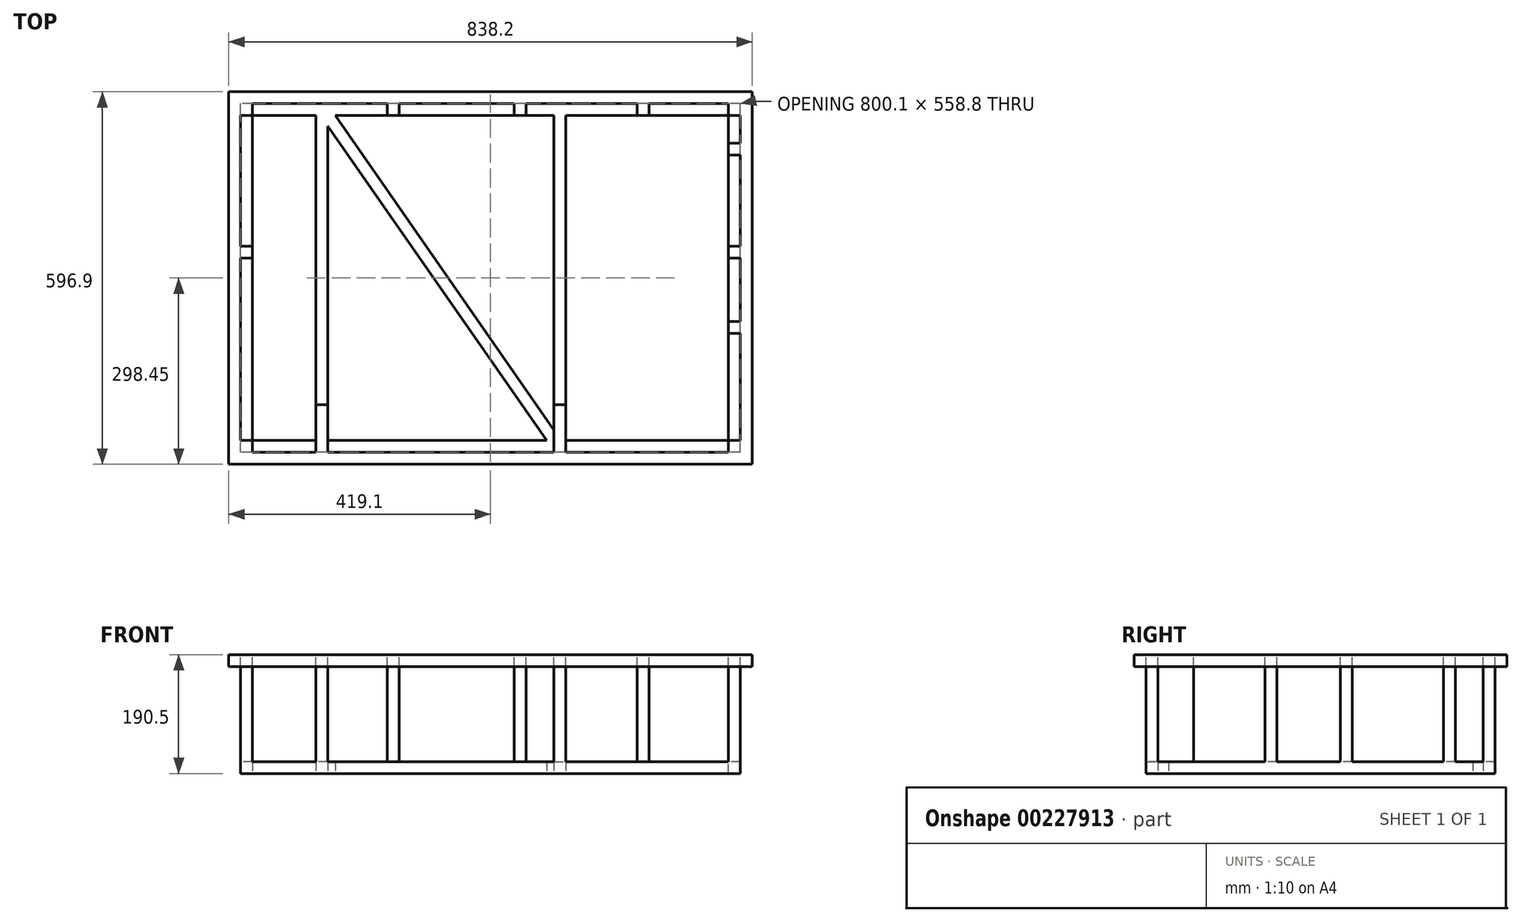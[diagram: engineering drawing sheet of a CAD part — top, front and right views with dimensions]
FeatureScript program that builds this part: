
annotation { "Feature Type Name" : "Feature", "Feature Type Description" : "" }
export const myFeature = defineFeature(function(context is Context, id is Id, definition is map)
    precondition{}
    {
        {
            var Q0;
            Q0=qCreatedBy(makeId("Top.planeOp"),FACE);
            var sketch = newSketch(context, id + "F0", { "sketchPlane" : qUnion([Q0])});
            skLineSegment(sketch, "E0.bottom", {"start": v(419.1, -298.45) * mm, "end": v(-419.1, -298.45) * mm});
            skLineSegment(sketch, "E0.top", {"start": v(419.1, 298.45) * mm, "end": v(-419.1, 298.45) * mm});
            skLineSegment(sketch, "E0.left", {"start": v(419.1, -298.45) * mm, "end": v(419.1, 298.45) * mm});
            skLineSegment(sketch, "E0.right", {"start": v(-419.1, -298.45) * mm, "end": v(-419.1, 298.45) * mm});
            skPoint(sketch, "E0.middle", {"position": v(0, 0) * mm});
            skSolve(sketch);
        }
        {
            var Q0;
            Q0=makeQuery(id+"F0.imprint","IMPRINT",FACE,{"disambiguationData":[TD([[makeQuery(id+"F0.imprint","IMPRINT",EDGE,{"derivedFrom":sQuery(id+"F0.wireOp",EDGE,"E0.bottom")}),-1.0]])]});
            extrude(context, id + "F1", {"entities" : qUnion([Q0]), "depth" : 19.05 * mm, "offsetDistance" : 25.4 * mm});
        }
        {
            var Q0;
            Q0=makeQuery(id+"F1.opExtrude","CAP_FACE",FACE,{"disambiguationData":[OSD([sQuery(id+"F0.wireOp",EDGE,"E0.bottom"),sQuery(id+"F0.wireOp",EDGE,"E0.top"),sQuery(id+"F0.wireOp",EDGE,"E0.left"),sQuery(id+"F0.wireOp",EDGE,"E0.right")])],"isStart":false});
            var sketch = newSketch(context, id + "F2", { "sketchPlane" : qUnion([Q0])});
            skLineSegment(sketch, "E1.0", {"start": v(400.05, -279.4) * mm, "end": v(-400.05, -279.4) * mm});
            skLineSegment(sketch, "E1.1", {"start": v(400.05, -279.4) * mm, "end": v(400.05, 279.4) * mm});
            skLineSegment(sketch, "E1.2", {"start": v(400.05, 279.4) * mm, "end": v(-400.05, 279.4) * mm});
            skLineSegment(sketch, "E1.3", {"start": v(-400.05, -279.4) * mm, "end": v(-400.05, 279.4) * mm});
            skSolve(sketch);
        }
        {
            var Q0;
            Q0=makeQuery(id+"F2.imprint","IMPRINT",FACE,{"disambiguationData":[TD([[makeQuery(id+"F2.imprint","IMPRINT",EDGE,{"derivedFrom":sQuery(id+"F2.wireOp",EDGE,"E1.0")}),-1.0]])]});
            extrude(context, id + "F3", {"entities" : qUnion([Q0]), "operationType" : NewBodyOperationType.REMOVE, "endBound" : BoundingType.THROUGH_ALL, "oppositeDirection" : true, "depth" : 25.4 * mm, "offsetDistance" : 25.4 * mm});
        }
        {
            var Q0;
            Q0=makeQuery(id+"F2.imprint","IMPRINT",FACE,{"disambiguationData":[TD([[makeQuery(id+"F2.imprint","IMPRINT",EDGE,{"derivedFrom":sQuery(id+"F2.wireOp",EDGE,"E1.0")}),-1.0]])]});
            var sketch = newSketch(context, id + "F4", { "sketchPlane" : qUnion([Q0])});
            skLineSegment(sketch, "E2.0", {"start": v(-381, -317.5) * mm, "end": v(-381, -260.35) * mm});
            skLineSegment(sketch, "E3.0", {"start": v(406.4, 260.35) * mm, "end": v(381, 260.35) * mm});
            skLineSegment(sketch, "E4.0", {"start": v(381, -317.5) * mm, "end": v(381, -260.35) * mm});
            skLineSegment(sketch, "E5.0", {"start": v(406.4, -260.35) * mm, "end": v(381, -260.35) * mm});
            skLineSegment(sketch, "E6.trimOffspring", {"start": v(-381, -260.35) * mm, "end": v(-406.4, -260.35) * mm});
            skLineSegment(sketch, "E7.trimOffspring", {"start": v(381, 260.35) * mm, "end": v(381, 317.5) * mm});
            skLineSegment(sketch, "E8.trimOffspring", {"start": v(-381, 260.35) * mm, "end": v(-406.4, 260.35) * mm});
            skLineSegment(sketch, "E9.trimOffspring", {"start": v(-381, 260.35) * mm, "end": v(-381, 317.5) * mm});
            skLineSegment(sketch, "E10.0", {"start": v(-177.8, -317.5) * mm, "end": v(-177.8, -298.45) * mm});
            skLineSegment(sketch, "E11.0", {"start": v(-158.75, -317.5) * mm, "end": v(-158.75, -298.45) * mm});
            skLineSegment(sketch, "E12", {"start": v(-177.8, -298.45) * mm, "end": v(-158.75, -298.45) * mm});
            skSolve(sketch);
        }
        {
            var Q0;
            {var subQ0=sQuery(id+"F4.wireOp",EDGE,"E8.trimOffspring");Q0=makeQuery(id+"F4.imprint","IMPRINT",FACE,{"disambiguationData":[TD([[makeQuery(id+"F4.imprint","IMPRINT",EDGE,{"derivedFrom":subQ0}),-1.0]])]});}
            var Q1;
            {var subQ0=sQuery(id+"F4.wireOp",EDGE,"E2.0");Q1=makeQuery(id+"F4.imprint","IMPRINT",FACE,{"disambiguationData":[TD([[makeQuery(id+"F4.imprint","IMPRINT",EDGE,{"derivedFrom":subQ0}),1.0]])]});}
            var Q2;
            {var subQ0=sQuery(id+"F4.wireOp",EDGE,"E3.0");Q2=makeQuery(id+"F4.imprint","IMPRINT",FACE,{"disambiguationData":[TD([[makeQuery(id+"F4.imprint","IMPRINT",EDGE,{"derivedFrom":subQ0}),-1.0]])]});}
            var Q3;
            {var subQ0=sQuery(id+"F4.wireOp",EDGE,"E4.0");Q3=makeQuery(id+"F4.imprint","IMPRINT",FACE,{"disambiguationData":[TD([[makeQuery(id+"F4.imprint","IMPRINT",EDGE,{"derivedFrom":subQ0}),-1.0]])]});}
            extrude(context, id + "F5", {"entities" : qUnion([Q0, Q1, Q2, Q3]), "operationType" : NewBodyOperationType.ADD, "oppositeDirection" : true, "depth" : 190.5 * mm, "offsetDistance" : 25.4 * mm});
        }
        {
            var Q0;
            Q0=makeQuery(id+"F2.imprint","IMPRINT",FACE,{"disambiguationData":[TD([[makeQuery(id+"F2.imprint","IMPRINT",EDGE,{"derivedFrom":sQuery(id+"F2.wireOp",EDGE,"E1.0")}),-1.0]])]});
            var sketch = newSketch(context, id + "F6", { "sketchPlane" : qUnion([Q0])});
            skLineSegment(sketch, "E13.left", {"start": v(-279.4, -203.2) * mm, "end": v(-279.4, -279.4) * mm});
            skLineSegment(sketch, "E13.right", {"start": v(-260.35, -203.2) * mm, "end": v(-260.35, -279.4) * mm});
            skLineSegment(sketch, "E14.0", {"start": v(-260.35, -203.2) * mm, "end": v(-279.4, -203.2) * mm});
            skLineSegment(sketch, "E15.0", {"start": v(406.4, -279.4) * mm, "end": v(-406.4, -279.4) * mm});
            skSolve(sketch);
        }
        {
            var Q0;
            Q0=makeQuery(id+"F6.imprint","IMPRINT",FACE,{"disambiguationData":[TD([[makeQuery(id+"F6.imprint","IMPRINT",EDGE,{"derivedFrom":sQuery(id+"F6.wireOp",EDGE,"E13.bottom")}),-1.0]])]});
            var Q1;
            {var subQ0=sQuery(id+"F6.wireOp",EDGE,"E13.left");Q1=makeQuery(id+"F6.imprint","IMPRINT",FACE,{"disambiguationData":[TD([[makeQuery(id+"F6.imprint","IMPRINT",EDGE,{"derivedFrom":subQ0}),1.0]])]});}
            extrude(context, id + "F7", {"entities" : qUnion([Q0, Q1]), "operationType" : NewBodyOperationType.ADD, "oppositeDirection" : true, "depth" : 190.5 * mm, "offsetDistance" : 25.4 * mm});
        }
        {
            var Q0;
            Q0=makeQuery(id+"F2.imprint","IMPRINT",FACE,{"disambiguationData":[TD([[makeQuery(id+"F2.imprint","IMPRINT",EDGE,{"derivedFrom":sQuery(id+"F2.wireOp",EDGE,"E1.0")}),1.0]])]});
            var sketch = newSketch(context, id + "F8", { "sketchPlane" : qUnion([Q0])});
            skLineSegment(sketch, "E16.0", {"start": v(-381, 31.75) * mm, "end": v(-381, 50.8) * mm});
            skLineSegment(sketch, "E17.0", {"start": v(406.4, 50.8) * mm, "end": v(381, 50.8) * mm});
            skLineSegment(sketch, "E18.0", {"start": v(381, 31.75) * mm, "end": v(381, 50.8) * mm});
            skLineSegment(sketch, "E19.0", {"start": v(19.05, -317.5) * mm, "end": v(19.05, 286.13) * mm});
            skLineSegment(sketch, "E20.0", {"start": v(406.4, 260.35) * mm, "end": v(381, 260.35) * mm});
            skLineSegment(sketch, "E21.0", {"start": v(406.4, 31.75) * mm, "end": v(381, 31.75) * mm});
            skLineSegment(sketch, "E22.0", {"start": v(0, -317.5) * mm, "end": v(0, 289.85) * mm});
            skLineSegment(sketch, "E23.trimOffspring", {"start": v(-381, 50.8) * mm, "end": v(-406.4, 50.8) * mm});
            skLineSegment(sketch, "E24.trimOffspring", {"start": v(-381, 260.35) * mm, "end": v(-381, 317.5) * mm});
            skLineSegment(sketch, "E25.trimOffspring", {"start": v(-381, 31.75) * mm, "end": v(-406.4, 31.75) * mm});
            skLineSegment(sketch, "E26.trimOffspring", {"start": v(-381, 260.35) * mm, "end": v(-406.4, 260.35) * mm});
            skLineSegment(sketch, "E27.trimOffspring", {"start": v(19.05, 260.35) * mm, "end": v(0, 260.35) * mm});
            skLineSegment(sketch, "E28.trimOffspring", {"start": v(19.05, 50.8) * mm, "end": v(0, 50.8) * mm});
            skLineSegment(sketch, "E29.trimOffspring", {"start": v(19.05, 31.75) * mm, "end": v(0, 31.75) * mm});
            skLineSegment(sketch, "E30.trimOffspring", {"start": v(381, 260.35) * mm, "end": v(381, 317.5) * mm});
            skSolve(sketch);
        }
        {
            var Q0;
            Q0=makeQuery(id+"F8.imprint","IMPRINT",FACE,{"disambiguationData":[TD([[makeQuery(id+"F8.imprint","IMPRINT",EDGE,{"derivedFrom":sQuery(id+"F8.wireOp",EDGE,"E16.0")}),1.0]])]});
            var Q1;
            {var subQ0=sQuery(id+"F8.wireOp",EDGE,"92bb0c61-4761-4d68-9f9f-d430d65edb0f.trimOffspring");Q1=makeQuery(id+"F8.imprint","IMPRINT",FACE,{"disambiguationData":[TD([[makeQuery(id+"F8.imprint","IMPRINT",EDGE,{"derivedFrom":subQ0}),-1.0]])]});}
            var Q2;
            {var subQ0=sQuery(id+"F8.wireOp",EDGE,"E17.0");Q2=makeQuery(id+"F8.imprint","IMPRINT",FACE,{"disambiguationData":[TD([[makeQuery(id+"F8.imprint","IMPRINT",EDGE,{"derivedFrom":subQ0}),1.0]])]});}
            extrude(context, id + "F9", {"entities" : qUnion([Q0, Q1, Q2]), "operationType" : NewBodyOperationType.ADD, "oppositeDirection" : true, "depth" : 190.5 * mm, "offsetDistance" : 25.4 * mm});
        }
        {
            var Q0;
            Q0=makeQuery(id+"F5.opExtrude","SWEPT_FACE",FACE,{"disambiguationData":[OSD([sQuery(id+"F4.wireOp",EDGE,"E8.trimOffspring")])]});
            var sketch = newSketch(context, id + "F10", { "sketchPlane" : qUnion([Q0])});
            skLineSegment(sketch, "E31.top", {"start": v(-381, -152.4) * mm, "end": v(-400.05, -152.4) * mm});
            skSolve(sketch);
        }
        {
            var Q0;
            Q0=makeQuery(id+"F5.opExtrude","SWEPT_FACE",FACE,{"disambiguationData":[OSD([sQuery(id+"F4.wireOp",EDGE,"E3.0")])]});
            var sketch = newSketch(context, id + "F11", { "sketchPlane" : qUnion([Q0])});
            skSolve(sketch);
        }
        {
            var Q0;
            {var subQ0=sQuery(id+"F10.wireOp",EDGE,"E31.top");Q0=makeQuery(id+"F10.imprint","IMPRINT",FACE,{"disambiguationData":[TD([[makeQuery(id+"F10.imprint","IMPRINT",EDGE,{"derivedFrom":subQ0}),1.0]])]});}
            var Q1;
            Q1=makeQuery(id+"FXD4YSxns08IY23_10.boolean.opBoolean","MERGE",FACE,{"derivedFrom":[makeQuery(id+"F5.opExtrude","SWEPT_FACE",FACE,{"disambiguationData":[OSD([sQuery(id+"F4.wireOp",EDGE,"E6.trimOffspring")])]}),makeQuery(id+"FXD4YSxns08IY23_10.opExtrude","SWEPT_FACE",FACE,{"disambiguationData":[OSD([sQuery(id+"F4.wireOp",EDGE,"E4.0"),sQuery(id+"F4.wireOp",EDGE,"E5.0")])]})]});
            extrude(context, id + "F12", {"entities" : qUnion([Q0]), "operationType" : NewBodyOperationType.ADD, "endBound" : BoundingType.UP_TO_SURFACE, "depth" : 25.4 * mm, "endBoundEntityFace" : qUnion([Q1]), "offsetDistance" : 25.4 * mm});
        }
        {
            var Q0;
            Q0=makeQuery(id+"F2.imprint","IMPRINT",FACE,{"disambiguationData":[TD([[makeQuery(id+"F2.imprint","IMPRINT",EDGE,{"derivedFrom":sQuery(id+"F2.wireOp",EDGE,"E1.0")}),-1.0]])]});
            var sketch = newSketch(context, id + "F13", { "sketchPlane" : qUnion([Q0])});
            skLineSegment(sketch, "E32.0", {"start": v(120.65, -317.5) * mm, "end": v(120.65, -203.2) * mm});
            skLineSegment(sketch, "E33.0", {"start": v(101.6, -317.5) * mm, "end": v(101.6, -203.2) * mm});
            skLineSegment(sketch, "E34.0", {"start": v(120.65, -203.2) * mm, "end": v(101.6, -203.2) * mm});
            skSolve(sketch);
        }
        {
            var Q0;
            {var subQ0=sQuery(id+"F13.wireOp",EDGE,"E32.0");Q0=makeQuery(id+"F13.imprint","IMPRINT",FACE,{"disambiguationData":[TD([[makeQuery(id+"F13.imprint","IMPRINT",EDGE,{"derivedFrom":subQ0}),1.0]])]});}
            var Q1;
            {var subQ0=sQuery(id+"F6.wireOp",EDGE,"E14.0");var subQ1=sQuery(id+"F4.wireOp",EDGE,"E8.trimOffspring");var subQ2=sQuery(id+"F4.wireOp",EDGE,"E4.0");var subQ3=sQuery(id+"F4.wireOp",EDGE,"E5.0");var subQ4=sQuery(id+"F8.wireOp",EDGE,"3b298be8-fb02-4c87-a49b-3ff32759ba27.trimOffspring");var subQ5=sQuery(id+"F4.wireOp",EDGE,"E9.trimOffspring");var subQ6=sQuery(id+"F2.wireOp",EDGE,"E1.2");var subQ7=sQuery(id+"F2.wireOp",EDGE,"E1.3");var subQ8=sQuery(id+"F2.wireOp",EDGE,"E1.1");var subQ9=sQuery(id+"F2.wireOp",EDGE,"E1.0");Q1=makeQuery(id+"FpkB6zeeMxbo54k_1.boolean.opBoolean","MERGE",FACE,{"derivedFrom":[makeQuery(id+"F12.boolean.opBoolean","MERGE",FACE,{"derivedFrom":[makeQuery(id+"F9.opExtrude","CAP_FACE",FACE,{"disambiguationData":[OSD([subQ7,sQuery(id+"F8.wireOp",EDGE,"E16.0"),sQuery(id+"F8.wireOp",EDGE,"E23.trimOffspring"),sQuery(id+"F8.wireOp",EDGE,"E25.trimOffspring")])],"isStart":false}),makeQuery(id+"FXD4YSxns08IY23_10.boolean.opBoolean","MERGE",FACE,{"derivedFrom":[makeQuery(id+"F5.opExtrude","CAP_FACE",FACE,{"disambiguationData":[OSD([subQ9,subQ7,sQuery(id+"F4.wireOp",EDGE,"E2.0"),sQuery(id+"F4.wireOp",EDGE,"E6.trimOffspring")])],"isStart":false}),makeQuery(id+"F7.opExtrude","CAP_FACE",FACE,{"disambiguationData":[OSD([sQuery(id+"F6.wireOp",EDGE,"E13.left"),sQuery(id+"F6.wireOp",EDGE,"E13.right"),subQ0,sQuery(id+"F6.wireOp",EDGE,"E15.0")])],"isStart":false}),makeQuery(id+"FrElrkVLBZXkbWn_13.boolean.opBoolean","MERGE",FACE,{"derivedFrom":[makeQuery(id+"F5.opExtrude","CAP_FACE",FACE,{"disambiguationData":[OSD([subQ9,subQ8,subQ2,subQ3])],"isStart":false}),makeQuery(id+"F9.opExtrude","CAP_FACE",FACE,{"disambiguationData":[OSD([subQ8,sQuery(id+"F8.wireOp",EDGE,"E17.0"),sQuery(id+"F8.wireOp",EDGE,"E18.0"),sQuery(id+"F8.wireOp",EDGE,"E21.0")])],"isStart":false}),makeQuery(id+"Fi0JkrTjfxZnNrc_13.boolean.opBoolean","MERGE",FACE,{"derivedFrom":[makeQuery(id+"F5.opExtrude","CAP_FACE",FACE,{"disambiguationData":[OSD([subQ8,subQ6,sQuery(id+"F4.wireOp",EDGE,"E3.0"),sQuery(id+"F4.wireOp",EDGE,"E7.trimOffspring")])],"isStart":false}),makeQuery(id+"FCnJRw7mSyagZAr_13.boolean.opBoolean","MERGE",FACE,{"derivedFrom":[makeQuery(id+"F5.opExtrude","CAP_FACE",FACE,{"disambiguationData":[OSD([subQ6,subQ7,subQ1,subQ5])],"isStart":false}),makeQuery(id+"F9.opExtrude","CAP_FACE",FACE,{"disambiguationData":[OSD([subQ6,sQuery(id+"F8.wireOp",EDGE,"92bb0c61-4761-4d68-9f9f-d430d65edb0f.trimOffspring"),subQ4,sQuery(id+"F8.wireOp",EDGE,"E27.trimOffspring")])],"isStart":false}),makeQuery(id+"FCnJRw7mSyagZAr_13.opExtrude","SWEPT_FACE",FACE,{"disambiguationData":[OSD([subQ5])]})]}),makeQuery(id+"Fi0JkrTjfxZnNrc_13.opExtrude","SWEPT_FACE",FACE,{"disambiguationData":[OSD([subQ4])]})]}),makeQuery(id+"FrElrkVLBZXkbWn_13.opExtrude","SWEPT_FACE",FACE,{"disambiguationData":[OSD([subQ3])]})]}),makeQuery(id+"FXD4YSxns08IY23_10.opExtrude","SWEPT_FACE",FACE,{"disambiguationData":[OSD([subQ2])]})]}),makeQuery(id+"F12.opExtrude","SWEPT_FACE",FACE,{"disambiguationData":[OSD([subQ1])]})]}),makeQuery(id+"FpkB6zeeMxbo54k_1.opExtrude","SWEPT_FACE",FACE,{"disambiguationData":[OSD([subQ0])]})]});}
            extrude(context, id + "F14", {"entities" : qUnion([Q0]), "operationType" : NewBodyOperationType.ADD, "endBound" : BoundingType.UP_TO_SURFACE, "oppositeDirection" : true, "depth" : 25.4 * mm, "endBoundEntityFace" : qUnion([Q1]), "offsetDistance" : 25.4 * mm});
        }
        {
            var Q0;
            Q0=makeQuery(id+"F2.imprint","IMPRINT",FACE,{"disambiguationData":[TD([[makeQuery(id+"F2.imprint","IMPRINT",EDGE,{"derivedFrom":sQuery(id+"F2.wireOp",EDGE,"E1.0")}),-1.0]])]});
            var sketch = newSketch(context, id + "F15", { "sketchPlane" : qUnion([Q0])});
            skLineSegment(sketch, "E35.0", {"start": v(381, -88.9) * mm, "end": v(381, -69.85) * mm});
            skLineSegment(sketch, "E36.0", {"start": v(400.05, -88.9) * mm, "end": v(381, -88.9) * mm});
            skLineSegment(sketch, "E37.0", {"start": v(400.05, -69.85) * mm, "end": v(381, -69.85) * mm});
            skLineSegment(sketch, "E38.0", {"start": v(400.05, 196.85) * mm, "end": v(381, 196.85) * mm});
            skLineSegment(sketch, "E39.0", {"start": v(400.05, 215.9) * mm, "end": v(381, 215.9) * mm});
            skLineSegment(sketch, "E40.trimOffspring", {"start": v(381, 196.85) * mm, "end": v(381, 215.9) * mm});
            skLineSegment(sketch, "E41.0", {"start": v(400.05, 196.85) * mm, "end": v(400.05, 215.9) * mm});
            skLineSegment(sketch, "E42.0", {"start": v(400.05, -88.9) * mm, "end": v(400.05, -69.85) * mm});
            skSolve(sketch);
        }
        {
            var Q0;
            {var subQ0=sQuery(id+"F4.wireOp",EDGE,"E3.0");Q0=makeQuery(id+"F11.imprint","IMPRINT",FACE,{"disambiguationData":[TD([[makeQuery(id+"F11.imprint","IMPRINT",EDGE,{"derivedFrom":makeQuery(id+"F5.opExtrude","CAP_EDGE",EDGE,{"disambiguationData":[OSD([subQ0])],"isStart":true})}),1.0]])]});}
            var sketch = newSketch(context, id + "F16", { "sketchPlane" : qUnion([Q0])});
            skLineSegment(sketch, "E43.0", {"start": v(400.05, -152.4) * mm, "end": v(381, -152.4) * mm});
            skSolve(sketch);
        }
        {
            var Q0;
            {var subQ0=sQuery(id+"F16.wireOp",EDGE,"E43.0");Q0=makeQuery(id+"F16.imprint","IMPRINT",FACE,{"disambiguationData":[TD([[makeQuery(id+"F16.imprint","IMPRINT",EDGE,{"derivedFrom":subQ0}),1.0]])]});}
            var Q1;
            Q1=makeQuery(id+"F5.opExtrude","SWEPT_FACE",FACE,{"disambiguationData":[OSD([sQuery(id+"F4.wireOp",EDGE,"E5.0")])]});
            extrude(context, id + "F17", {"entities" : qUnion([Q0]), "operationType" : NewBodyOperationType.ADD, "endBound" : BoundingType.UP_TO_SURFACE, "depth" : 25.4 * mm, "endBoundEntityFace" : qUnion([Q1]), "offsetDistance" : 25.4 * mm});
        }
        {
            var Q0;
            {var subQ0=sQuery(id+"F4.wireOp",EDGE,"E9.trimOffspring");Q0=makeQuery(id+"F12.boolean.opBoolean","MERGE",FACE,{"derivedFrom":[makeQuery(id+"F5.opExtrude","SWEPT_FACE",FACE,{"disambiguationData":[OSD([sQuery(id+"F4.wireOp",EDGE,"E2.0")])]}),makeQuery(id+"F5.opExtrude","SWEPT_FACE",FACE,{"disambiguationData":[OSD([subQ0])]}),makeQuery(id+"F9.opExtrude","SWEPT_FACE",FACE,{"disambiguationData":[OSD([sQuery(id+"F8.wireOp",EDGE,"E16.0")])]}),makeQuery(id+"F12.opExtrude","SWEPT_FACE",FACE,{"disambiguationData":[OSD([sQuery(id+"F4.wireOp",EDGE,"E8.trimOffspring"),subQ0])]})]});}
            var sketch = newSketch(context, id + "F18", { "sketchPlane" : qUnion([Q0])});
            skLineSegment(sketch, "E44.0", {"start": v(260.35, -152.4) * mm, "end": v(279.4, -152.4) * mm});
            skLineSegment(sketch, "E45.0", {"start": v(260.35, -171.45) * mm, "end": v(260.35, -152.4) * mm});
            skSolve(sketch);
        }
        {
            var Q0;
            {var subQ0=sQuery(id+"F18.wireOp",EDGE,"E44.0");Q0=makeQuery(id+"F18.imprint","IMPRINT",FACE,{"disambiguationData":[TD([[makeQuery(id+"F18.imprint","IMPRINT",EDGE,{"derivedFrom":subQ0}),-1.0]])]});}
            var Q1;
            {var subQ0=sQuery(id+"F4.wireOp",EDGE,"E7.trimOffspring");Q1=makeQuery(id+"F17.boolean.opBoolean","MERGE",FACE,{"derivedFrom":[makeQuery(id+"F5.opExtrude","SWEPT_FACE",FACE,{"disambiguationData":[OSD([sQuery(id+"F4.wireOp",EDGE,"E4.0")])]}),makeQuery(id+"F5.opExtrude","SWEPT_FACE",FACE,{"disambiguationData":[OSD([subQ0])]}),makeQuery(id+"F9.opExtrude","SWEPT_FACE",FACE,{"disambiguationData":[OSD([sQuery(id+"F8.wireOp",EDGE,"E18.0")])]}),makeQuery(id+"F17.opExtrude","SWEPT_FACE",FACE,{"disambiguationData":[OSD([sQuery(id+"F4.wireOp",EDGE,"E3.0"),subQ0])]})]});}
            extrude(context, id + "F19", {"entities" : qUnion([Q0]), "operationType" : NewBodyOperationType.ADD, "endBound" : BoundingType.UP_TO_SURFACE, "depth" : 25.4 * mm, "endBoundEntityFace" : qUnion([Q1]), "offsetDistance" : 25.4 * mm});
        }
        {
            var Q0;
            {var subQ1=sQuery(id+"F2.wireOp",EDGE,"E1.0");var subQ3=sQuery(id+"F4.wireOp",EDGE,"E4.0");var subQ5=sQuery(id+"F8.wireOp",EDGE,"E18.0");var subQ19=sQuery(id+"F4.wireOp",EDGE,"E7.trimOffspring");var subQ20=makeQuery(id+"F5.opExtrude","SWEPT_FACE",FACE,{"disambiguationData":[OSD([subQ19])]});var subQ23=makeQuery(id+"F5.opExtrude","SWEPT_FACE",FACE,{"disambiguationData":[OSD([subQ3])]});var subQ24=sQuery(id+"F4.wireOp",EDGE,"E3.0");var subQ25=makeQuery(id+"F9.opExtrude","SWEPT_FACE",FACE,{"disambiguationData":[OSD([subQ5])]});var subQ26=makeQuery(id+"F17.opExtrude","SWEPT_FACE",FACE,{"disambiguationData":[OSD([subQ24,subQ19])]});Q0=makeQuery(id+"F19.boolean.opBoolean","SPLIT",FACE,{"disambiguationData":[TD([makeQuery(id+"F3.boolean.opBoolean","COPY",FACE,{"derivedFrom":makeQuery(id+"F3.opExtrude","SWEPT_FACE",FACE,{"disambiguationData":[OSD([subQ1])]})})])],"derivedFrom":makeQuery(id+"F17.boolean.opBoolean","MERGE",FACE,{"derivedFrom":[subQ23,subQ20,subQ25,subQ26]})});}
            var sketch = newSketch(context, id + "F20", { "sketchPlane" : qUnion([Q0])});
            skLineSegment(sketch, "E46.0", {"start": v(279.4, -152.4) * mm, "end": v(260.35, -152.4) * mm});
            skLineSegment(sketch, "E47.0", {"start": v(260.35, -171.45) * mm, "end": v(260.35, -152.4) * mm});
            skSolve(sketch);
        }
        {
            var Q0;
            {var subQ0=sQuery(id+"F20.wireOp",EDGE,"E46.0");Q0=makeQuery(id+"F20.imprint","IMPRINT",FACE,{"disambiguationData":[TD([[makeQuery(id+"F20.imprint","IMPRINT",EDGE,{"derivedFrom":subQ0}),1.0]])]});}
            var Q1;
            {var subQ0=sQuery(id+"F8.wireOp",EDGE,"E16.0");var subQ1=makeQuery(id+"F9.opExtrude","SWEPT_FACE",FACE,{"disambiguationData":[OSD([subQ0])]});var subQ2=sQuery(id+"F4.wireOp",EDGE,"E8.trimOffspring");var subQ4=sQuery(id+"F2.wireOp",EDGE,"E1.0");var subQ6=sQuery(id+"F4.wireOp",EDGE,"E2.0");var subQ11=sQuery(id+"F4.wireOp",EDGE,"E9.trimOffspring");var subQ12=makeQuery(id+"F5.opExtrude","SWEPT_FACE",FACE,{"disambiguationData":[OSD([subQ11])]});var subQ23=makeQuery(id+"F5.opExtrude","SWEPT_FACE",FACE,{"disambiguationData":[OSD([subQ6])]});var subQ26=makeQuery(id+"F12.opExtrude","SWEPT_FACE",FACE,{"disambiguationData":[OSD([subQ2,subQ11])]});Q1=makeQuery(id+"F19.boolean.opBoolean","SPLIT",FACE,{"disambiguationData":[TD([makeQuery(id+"F3.boolean.opBoolean","COPY",FACE,{"derivedFrom":makeQuery(id+"F3.opExtrude","SWEPT_FACE",FACE,{"disambiguationData":[OSD([subQ4])]})})])],"derivedFrom":makeQuery(id+"F12.boolean.opBoolean","MERGE",FACE,{"derivedFrom":[subQ23,subQ12,subQ1,subQ26]})});}
            extrude(context, id + "F21", {"entities" : qUnion([Q0]), "operationType" : NewBodyOperationType.ADD, "endBound" : BoundingType.UP_TO_SURFACE, "depth" : 25.4 * mm, "endBoundEntityFace" : qUnion([Q1]), "offsetDistance" : 25.4 * mm});
        }
        {
            var Q0;
            Q0=makeQuery(id+"F15.imprint","IMPRINT",FACE,{"disambiguationData":[TD([[makeQuery(id+"F15.imprint","IMPRINT",EDGE,{"derivedFrom":sQuery(id+"F15.wireOp",EDGE,"E35.0")}),-1.0]])]});
            var Q1;
            {var subQ2=sQuery(id+"F4.wireOp",EDGE,"E5.0");Q1=makeQuery(id+"F17.boolean.opBoolean","SPLIT",FACE,{"disambiguationData":[TD([makeQuery(id+"F5.opExtrude","SWEPT_FACE",FACE,{"disambiguationData":[OSD([subQ2])]})])],"derivedFrom":makeQuery(id+"F17.opExtrude","SWEPT_FACE",FACE,{"disambiguationData":[OSD([sQuery(id+"F16.wireOp",EDGE,"E43.0")])]})});}
            extrude(context, id + "F22", {"entities" : qUnion([Q0, Q1]), "operationType" : NewBodyOperationType.ADD, "endBound" : BoundingType.UP_TO_NEXT, "oppositeDirection" : true, "depth" : 25.4 * mm, "offsetDistance" : 25.4 * mm});
        }
        {
            var Q0;
            Q0 = qSketchRegion(id + "F15", true);
            extrude(context, id + "F23", {"entities" : qUnion([Q0]), "operationType" : NewBodyOperationType.ADD, "endBound" : BoundingType.UP_TO_NEXT, "oppositeDirection" : true, "depth" : 25.4 * mm, "offsetDistance" : 25.4 * mm});
        }
        {
            var Q0;
            Q0=makeQuery(id+"F14.opExtrude","SWEPT_FACE",FACE,{"disambiguationData":[OSD([sQuery(id+"F13.wireOp",EDGE,"E34.0")])]});
            var sketch = newSketch(context, id + "F24", { "sketchPlane" : qUnion([Q0])});
            skLineSegment(sketch, "E48.0", {"start": v(-101.6, -152.4) * mm, "end": v(-120.65, -152.4) * mm});
            skSolve(sketch);
        }
        {
            var Q0;
            {var subQ0=sQuery(id+"F24.wireOp",EDGE,"E48.0");Q0=makeQuery(id+"F24.imprint","IMPRINT",FACE,{"disambiguationData":[TD([[makeQuery(id+"F24.imprint","IMPRINT",EDGE,{"derivedFrom":subQ0}),1.0]])]});}
            extrude(context, id + "F25", {"entities" : qUnion([Q0]), "operationType" : NewBodyOperationType.ADD, "endBound" : BoundingType.UP_TO_NEXT, "depth" : 25.4 * mm, "offsetDistance" : 25.4 * mm});
        }
        {
            var Q0;
            Q0=makeQuery(id+"F7.opExtrude","SWEPT_FACE",FACE,{"disambiguationData":[OSD([sQuery(id+"F6.wireOp",EDGE,"E14.0")])]});
            var sketch = newSketch(context, id + "F26", { "sketchPlane" : qUnion([Q0])});
            skLineSegment(sketch, "E49.0", {"start": v(260.35, -152.4) * mm, "end": v(279.4, -152.4) * mm});
            skSolve(sketch);
        }
        {
            var Q0;
            {var subQ0=sQuery(id+"F26.wireOp",EDGE,"E49.0");Q0=makeQuery(id+"F26.imprint","IMPRINT",FACE,{"disambiguationData":[TD([[makeQuery(id+"F26.imprint","IMPRINT",EDGE,{"derivedFrom":subQ0}),-1.0]])]});}
            extrude(context, id + "F27", {"entities" : qUnion([Q0]), "operationType" : NewBodyOperationType.ADD, "endBound" : BoundingType.UP_TO_NEXT, "depth" : 25.4 * mm, "offsetDistance" : 25.4 * mm});
        }
        {
            var Q0;
            Q0=makeQuery(id+"F2.imprint","IMPRINT",FACE,{"disambiguationData":[TD([[makeQuery(id+"F2.imprint","IMPRINT",EDGE,{"derivedFrom":sQuery(id+"F2.wireOp",EDGE,"E1.0")}),-1.0]])]});
            var sketch = newSketch(context, id + "F28", { "sketchPlane" : qUnion([Q0])});
            skLineSegment(sketch, "E50.0", {"start": v(254, 260.35) * mm, "end": v(234.95, 260.35) * mm});
            skLineSegment(sketch, "E51.0", {"start": v(-165.1, 260.35) * mm, "end": v(-165.1, 279.4) * mm});
            skLineSegment(sketch, "E52.0", {"start": v(-146.05, 260.35) * mm, "end": v(-146.05, 279.4) * mm});
            skLineSegment(sketch, "E53.0", {"start": v(254, 260.35) * mm, "end": v(254, 279.4) * mm});
            skLineSegment(sketch, "E54.0", {"start": v(234.95, 260.35) * mm, "end": v(234.95, 279.4) * mm});
            skLineSegment(sketch, "E55.0", {"start": v(57.15, 260.35) * mm, "end": v(57.15, 279.4) * mm});
            skLineSegment(sketch, "E56.0", {"start": v(38.1, 260.35) * mm, "end": v(38.1, 279.4) * mm});
            skLineSegment(sketch, "E57.trimOffspring", {"start": v(-146.05, 260.35) * mm, "end": v(-165.1, 260.35) * mm});
            skLineSegment(sketch, "E58.trimOffspring", {"start": v(57.15, 260.35) * mm, "end": v(38.1, 260.35) * mm});
            skSolve(sketch);
        }
        {
            var Q0;
            {var subQ0=sQuery(id+"F28.wireOp",EDGE,"E51.0");Q0=makeQuery(id+"F28.imprint","IMPRINT",FACE,{"disambiguationData":[TD([[makeQuery(id+"F28.imprint","IMPRINT",EDGE,{"derivedFrom":subQ0}),-1.0]])]});}
            var Q1;
            {var subQ0=sQuery(id+"F28.wireOp",EDGE,"E55.0");Q1=makeQuery(id+"F28.imprint","IMPRINT",FACE,{"disambiguationData":[TD([[makeQuery(id+"F28.imprint","IMPRINT",EDGE,{"derivedFrom":subQ0}),1.0]])]});}
            var Q2;
            Q2=makeQuery(id+"F28.imprint","IMPRINT",FACE,{"disambiguationData":[TD([[makeQuery(id+"F28.imprint","IMPRINT",EDGE,{"derivedFrom":sQuery(id+"F28.wireOp",EDGE,"E50.0")}),-1.0]])]});
            extrude(context, id + "F29", {"entities" : qUnion([Q0, Q1, Q2]), "operationType" : NewBodyOperationType.ADD, "endBound" : BoundingType.UP_TO_NEXT, "oppositeDirection" : true, "depth" : 25.4 * mm, "offsetDistance" : 25.4 * mm});
        }
        {
            var Q0;
            {var subQ0=sQuery(id+"F6.wireOp",EDGE,"E14.0");var subQ1=sQuery(id+"F8.wireOp",EDGE,"E25.trimOffspring");var subQ2=sQuery(id+"F8.wireOp",EDGE,"E23.trimOffspring");var subQ3=sQuery(id+"F8.wireOp",EDGE,"E16.0");var subQ4=sQuery(id+"F4.wireOp",EDGE,"E9.trimOffspring");var subQ5=sQuery(id+"F4.wireOp",EDGE,"E8.trimOffspring");var subQ6=sQuery(id+"F4.wireOp",EDGE,"E6.trimOffspring");var subQ7=sQuery(id+"F4.wireOp",EDGE,"E2.0");var subQ8=sQuery(id+"F2.wireOp",EDGE,"E1.3");var subQ9=sQuery(id+"F2.wireOp",EDGE,"E1.2");var subQ10=sQuery(id+"F2.wireOp",EDGE,"E1.0");var subQ11=sQuery(id+"F8.wireOp",EDGE,"E18.0");var subQ12=sQuery(id+"F4.wireOp",EDGE,"E7.trimOffspring");var subQ13=sQuery(id+"F4.wireOp",EDGE,"E4.0");var subQ14=sQuery(id+"F4.wireOp",EDGE,"E3.0");var subQ15=sQuery(id+"F2.wireOp",EDGE,"E1.1");Q0=makeQuery(id+"F27.boolean.opBoolean","MERGE",FACE,{"derivedFrom":[makeQuery(id+"F25.boolean.opBoolean","MERGE",FACE,{"derivedFrom":[makeQuery(id+"F21.boolean.opBoolean","MERGE",FACE,{"derivedFrom":[makeQuery(id+"F7.opExtrude","CAP_FACE",FACE,{"disambiguationData":[OSD([sQuery(id+"F6.wireOp",EDGE,"E13.left"),sQuery(id+"F6.wireOp",EDGE,"E13.right"),subQ0,sQuery(id+"F6.wireOp",EDGE,"E15.0")])],"isStart":false}),makeQuery(id+"F14.opExtrude","CAP_FACE",FACE,{"disambiguationData":[OSD([subQ10,subQ9,subQ8,subQ7,subQ6,subQ5,subQ4,subQ3,subQ2,subQ1])],"isStart":false}),makeQuery(id+"F19.boolean.opBoolean","MERGE",FACE,{"derivedFrom":[makeQuery(id+"F12.boolean.opBoolean","MERGE",FACE,{"derivedFrom":[makeQuery(id+"F5.opExtrude","CAP_FACE",FACE,{"disambiguationData":[OSD([subQ10,subQ8,subQ7,subQ6])],"isStart":false}),makeQuery(id+"F5.opExtrude","CAP_FACE",FACE,{"disambiguationData":[OSD([subQ9,subQ8,subQ5,subQ4])],"isStart":false}),makeQuery(id+"F9.opExtrude","CAP_FACE",FACE,{"disambiguationData":[OSD([subQ8,subQ3,subQ2,subQ1])],"isStart":false}),makeQuery(id+"F12.opExtrude","SWEPT_FACE",FACE,{"disambiguationData":[OSD([subQ5])]})]}),makeQuery(id+"F17.boolean.opBoolean","MERGE",FACE,{"derivedFrom":[makeQuery(id+"F5.opExtrude","CAP_FACE",FACE,{"disambiguationData":[OSD([subQ15,subQ9,subQ14,subQ12])],"isStart":false}),makeQuery(id+"F5.opExtrude","CAP_FACE",FACE,{"disambiguationData":[OSD([subQ10,subQ15,subQ13,sQuery(id+"F4.wireOp",EDGE,"E5.0")])],"isStart":false}),makeQuery(id+"F9.opExtrude","CAP_FACE",FACE,{"disambiguationData":[OSD([subQ15,sQuery(id+"F8.wireOp",EDGE,"E17.0"),subQ11,sQuery(id+"F8.wireOp",EDGE,"E21.0")])],"isStart":false}),makeQuery(id+"F17.opExtrude","SWEPT_FACE",FACE,{"disambiguationData":[OSD([subQ14])]})]}),makeQuery(id+"F19.opExtrude","SWEPT_FACE",FACE,{"disambiguationData":[OSD([subQ7,subQ5,subQ4,subQ3])]})]}),makeQuery(id+"F21.opExtrude","SWEPT_FACE",FACE,{"disambiguationData":[OSD([subQ14,subQ13,subQ12,subQ11])]})]}),makeQuery(id+"F25.opExtrude","SWEPT_FACE",FACE,{"disambiguationData":[OSD([subQ10,subQ9,subQ8,subQ7,subQ6,subQ5,subQ4,subQ3,subQ2,subQ1,sQuery(id+"F13.wireOp",EDGE,"E34.0")])]})]}),makeQuery(id+"F27.opExtrude","SWEPT_FACE",FACE,{"disambiguationData":[OSD([subQ0])]})]});}
            var sketch = newSketch(context, id + "F30", { "sketchPlane" : qUnion([Q0])});
            skLineSegment(sketch, "E59.0", {"start": v(-268.17, -254.91) * mm, "end": v(93.78, 265.79) * mm});
            skLineSegment(sketch, "E60.0", {"start": v(-252.53, -265.79) * mm, "end": v(109.42, 254.91) * mm});
            skSolve(sketch);
        }
        {
            var Q0;
            {var subQ26=sQuery(id+"F6.wireOp",EDGE,"E14.0");var subQ27=sQuery(id+"F6.wireOp",EDGE,"E13.right");var subQ45=sQuery(id+"F30.wireOp",EDGE,"E59.0");var subQ47=makeQuery(id+"F27.boolean.opBoolean","MERGE",EDGE,{"derivedFrom":[makeQuery(id+"F7.opExtrude","CAP_EDGE",EDGE,{"disambiguationData":[OSD([subQ27])],"isStart":false}),makeQuery(id+"F27.opExtrude","SWEPT_EDGE",EDGE,{"disambiguationData":[OSD([subQ27,subQ26])]})]});var subQ48=makeQuery(id+"F30.imprint","INTERSECT",VERTEX,{"derivedFrom":[subQ47,subQ45]});Q0=makeQuery(id+"F30.imprint","IMPRINT",FACE,{"disambiguationData":[TD([[makeQuery(id+"F30.imprint","IMPRINT",EDGE,{"disambiguationData":[TD([[subQ48,-1.0]])],"derivedFrom":subQ45}),-1.0]])]});}
            var Q1;
            Q1=makeQuery(id+"F21.boolean.opBoolean","SPLIT",FACE,{"disambiguationData":[TD([makeQuery(id+"F7.opExtrude","SWEPT_FACE",FACE,{"disambiguationData":[OSD([sQuery(id+"F6.wireOp",EDGE,"E13.right")])]})])],"derivedFrom":makeQuery(id+"F21.opExtrude","SWEPT_FACE",FACE,{"disambiguationData":[OSD([sQuery(id+"F20.wireOp",EDGE,"E46.0")])]})});
            extrude(context, id + "F31", {"entities" : qUnion([Q0]), "operationType" : NewBodyOperationType.ADD, "endBound" : BoundingType.UP_TO_SURFACE, "oppositeDirection" : true, "depth" : 25.4 * mm, "endBoundEntityFace" : qUnion([Q1]), "offsetDistance" : 25.4 * mm});
        }
    });
